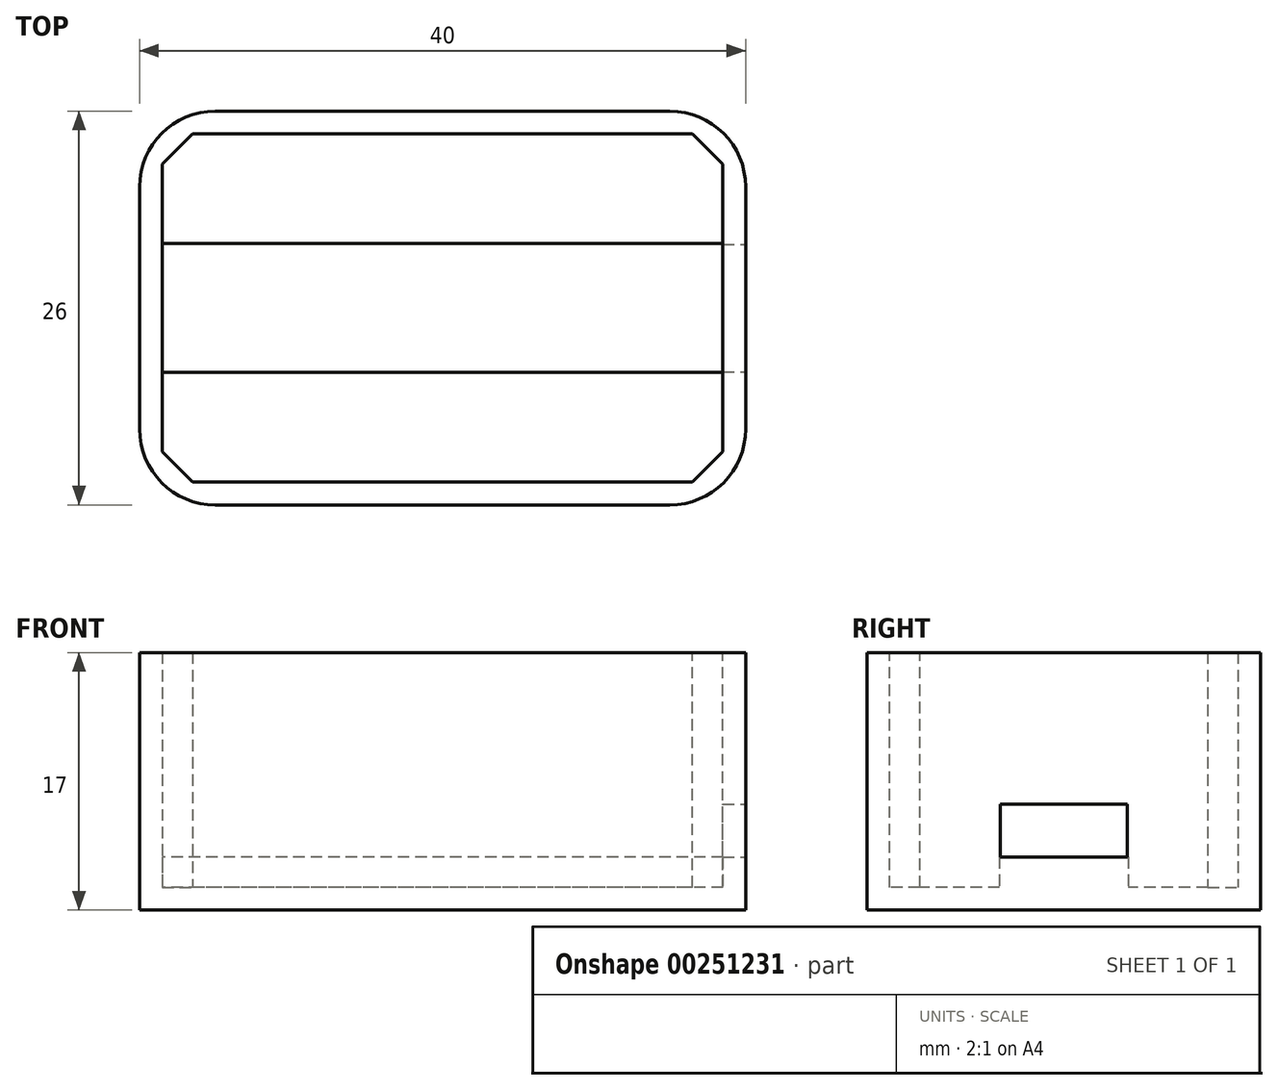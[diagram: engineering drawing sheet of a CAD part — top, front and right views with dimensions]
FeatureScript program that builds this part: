
annotation { "Feature Type Name" : "Feature", "Feature Type Description" : "" }
export const myFeature = defineFeature(function(context is Context, id is Id, definition is map)
    precondition{}
    {
        {
            var Q0;
            Q0=qCreatedBy(makeId("Top.planeOp"),FACE);
            var sketch = newSketch(context, id + "F0", { "sketchPlane" : qUnion([Q0])});
            skLineSegment(sketch, "E0.bottom", {"start": v(20, 13) * mm, "end": v(-20, 13) * mm});
            skLineSegment(sketch, "E0.top", {"start": v(20, -13) * mm, "end": v(-20, -13) * mm});
            skLineSegment(sketch, "E0.left", {"start": v(20, 13) * mm, "end": v(20, -13) * mm});
            skLineSegment(sketch, "E0.right", {"start": v(-20, 13) * mm, "end": v(-20, -13) * mm});
            skPoint(sketch, "E0.middle", {"position": v(0, 0) * mm});
            skSolve(sketch);
        }
        {
            var Q0;
            Q0 = qSketchRegion(id + "F0", true);
            extrude(context, id + "F1", {"entities" : qUnion([Q0]), "depth" : 17 * mm});
        }
        {
            var Q0;
            Q0=makeQuery(id+"F1.opExtrude","CAP_FACE",FACE,{"disambiguationData":[OSD([sQuery(id+"F0.wireOp",EDGE,"E0.bottom"),sQuery(id+"F0.wireOp",EDGE,"E0.top"),sQuery(id+"F0.wireOp",EDGE,"E0.left"),sQuery(id+"F0.wireOp",EDGE,"E0.right")])],"isStart":false});
            shell(context, id + "F2", {"entities" : qUnion([Q0]), "thickness" : 1.5 * mm});
        }
        {
            var Q0;
            Q0=makeQuery(id+"F2.opShell","OFFSET_FACE",FACE,{"disambiguationData":[OSD([sQuery(id+"F0.wireOp",EDGE,"E0.bottom"),sQuery(id+"F0.wireOp",EDGE,"E0.top"),sQuery(id+"F0.wireOp",EDGE,"E0.left"),sQuery(id+"F0.wireOp",EDGE,"E0.right")])]});
            var sketch = newSketch(context, id + "F3", { "sketchPlane" : qUnion([Q0])});
            skLineSegment(sketch, "E1.bottom", {"start": v(18.5, 4.25) * mm, "end": v(-18.5, 4.25) * mm});
            skLineSegment(sketch, "E1.top", {"start": v(18.5, -4.25) * mm, "end": v(-18.5, -4.25) * mm});
            skLineSegment(sketch, "E1.left", {"start": v(18.5, 4.25) * mm, "end": v(18.5, -4.25) * mm});
            skLineSegment(sketch, "E1.right", {"start": v(-18.5, 4.25) * mm, "end": v(-18.5, -4.25) * mm});
            skPoint(sketch, "E1.middle", {"position": v(0, 0) * mm});
            skSolve(sketch);
        }
        {
            var Q0;
            Q0 = qSketchRegion(id + "F3", true);
            extrude(context, id + "F4", {"entities" : qUnion([Q0]), "operationType" : NewBodyOperationType.ADD, "depth" : 2 * mm});
        }
        {
            var Q0;
            Q0=makeQuery(id+"F1.opExtrude","SWEPT_FACE",FACE,{"disambiguationData":[OSD([sQuery(id+"F0.wireOp",EDGE,"E0.left")])]});
            var sketch = newSketch(context, id + "F5", { "sketchPlane" : qUnion([Q0])});
            skLineSegment(sketch, "E2.bottom", {"start": v(4.2, 7) * mm, "end": v(-4.2, 7) * mm});
            skLineSegment(sketch, "E2.top", {"start": v(4.2, 3.5) * mm, "end": v(-4.2, 3.5) * mm});
            skLineSegment(sketch, "E2.left", {"start": v(4.2, 7) * mm, "end": v(4.2, 3.5) * mm});
            skLineSegment(sketch, "E2.right", {"start": v(-4.2, 7) * mm, "end": v(-4.2, 3.5) * mm});
            skPoint(sketch, "E2.middle", {"position": v(0, 5.25) * mm});
            skSolve(sketch);
        }
        {
            var Q0;
            Q0 = qSketchRegion(id + "F5", true);
            extrude(context, id + "F6", {"entities" : qUnion([Q0]), "operationType" : NewBodyOperationType.REMOVE, "endBound" : BoundingType.UP_TO_NEXT, "oppositeDirection" : true, "depth" : 25 * mm});
        }
        {
            var Q0;
            Q0=makeQuery(id+"F2.opShell","OFFSET_EDGE",EDGE,{"disambiguationData":[OSD([sQuery(id+"F0.wireOp",EDGE,"E0.bottom"),sQuery(id+"F0.wireOp",EDGE,"E0.right")])]});
            var Q1;
            Q1=makeQuery(id+"F2.opShell","OFFSET_EDGE",EDGE,{"disambiguationData":[OSD([sQuery(id+"F0.wireOp",EDGE,"E0.bottom"),sQuery(id+"F0.wireOp",EDGE,"E0.left")])]});
            var Q2;
            Q2=makeQuery(id+"F2.opShell","OFFSET_EDGE",EDGE,{"disambiguationData":[OSD([sQuery(id+"F0.wireOp",EDGE,"E0.top"),sQuery(id+"F0.wireOp",EDGE,"E0.left")])]});
            var Q3;
            Q3=makeQuery(id+"F2.opShell","OFFSET_EDGE",EDGE,{"disambiguationData":[OSD([sQuery(id+"F0.wireOp",EDGE,"E0.top"),sQuery(id+"F0.wireOp",EDGE,"E0.right")])]});
            chamfer(context, id + "F7", {"entities" : qUnion([Q0, Q1, Q2, Q3]), "width" : 2 * mm, "tangentPropagation" : true});
        }
        {
            var Q0;
            Q0=makeQuery(id+"F1.opExtrude","SWEPT_EDGE",EDGE,{"disambiguationData":[OSD([sQuery(id+"F0.wireOp",EDGE,"E0.bottom"),sQuery(id+"F0.wireOp",EDGE,"E0.right")])]});
            var Q1;
            Q1=makeQuery(id+"F1.opExtrude","SWEPT_EDGE",EDGE,{"disambiguationData":[OSD([sQuery(id+"F0.wireOp",EDGE,"E0.bottom"),sQuery(id+"F0.wireOp",EDGE,"E0.left")])]});
            var Q2;
            Q2=makeQuery(id+"F1.opExtrude","SWEPT_EDGE",EDGE,{"disambiguationData":[OSD([sQuery(id+"F0.wireOp",EDGE,"E0.top"),sQuery(id+"F0.wireOp",EDGE,"E0.left")])]});
            var Q3;
            Q3=makeQuery(id+"F1.opExtrude","SWEPT_EDGE",EDGE,{"disambiguationData":[OSD([sQuery(id+"F0.wireOp",EDGE,"E0.top"),sQuery(id+"F0.wireOp",EDGE,"E0.right")])]});
            fillet(context, id + "F8", {"entities" : qUnion([Q0, Q1, Q2, Q3]), "radius" : 5 * mm, "tangentPropagation" : true, "allowEdgeOverflow" : false});
        }
    });
